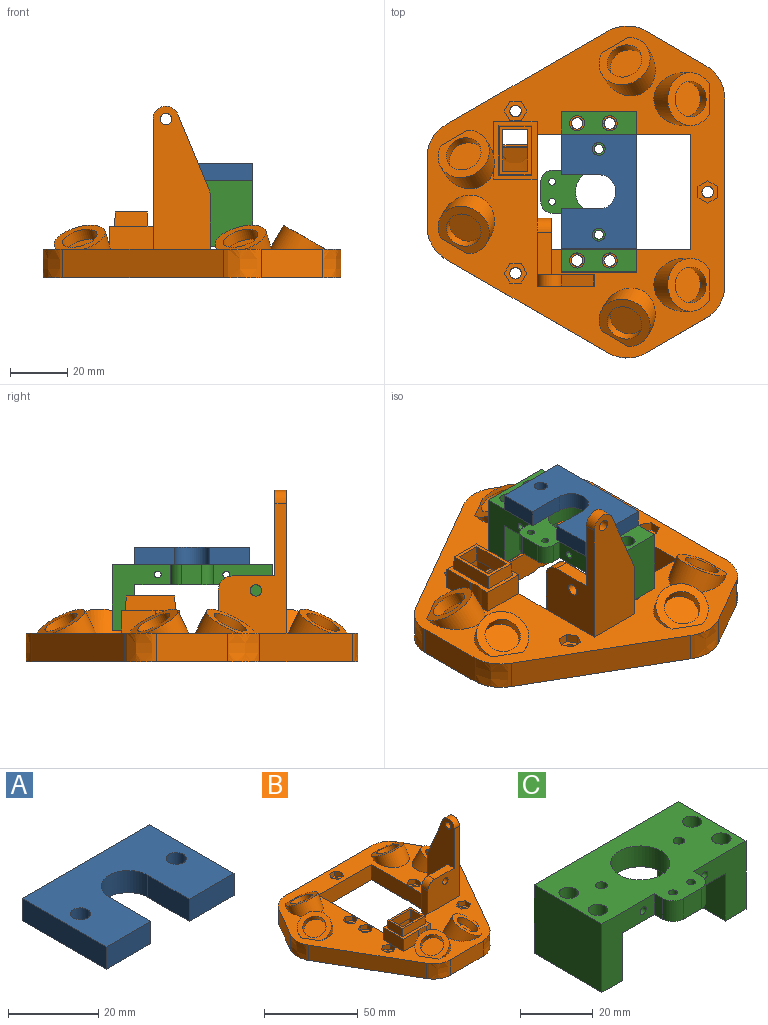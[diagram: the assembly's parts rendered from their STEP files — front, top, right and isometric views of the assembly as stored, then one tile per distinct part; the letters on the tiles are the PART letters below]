
ASSEMBLY  parts=3 mates=1
PART A: 12 faces, bbox 40x26.4x6 mm
  f0: plane 26.4x6mm, normal (1,0,0), area 158.4mm2, adj f1,f9,f10,f11
  f1: plane 40x6mm, normal (0,1,0), area 240mm2, adj f0,f2,f10,f11
  f2: plane 26.4x6mm, normal (-1,0,0), area 158.4mm2, adj f1,f3,f10,f11
  f3: plane 14x6mm, normal (0,-1,0), area 84mm2, adj f2,f4,f10,f11
  f4: plane 13.1x6mm, normal (1,0,0), area 78.6mm2, adj f3,f5,f10,f11
  f5: cylinder r=6mm len=12mm, axis (0,0,-1), area 113.1mm2, adj f4,f6,f10,f11
  f6: plane 13.1x6mm, normal (-1,0,0), area 78.6mm2, adj f5,f9,f10,f11
  f7: cylinder r=2.25mm len=6mm, axis (0,0,-1), area 84.8mm2, adj f10,f11
  f8: cylinder r=2.25mm len=6mm, axis (0,0,-1), area 84.8mm2, adj f10,f11
  f9: plane 14x6mm, normal (0,-1,0), area 84mm2, adj f0,f6,f10,f11
  f10: plane 40x26.4mm, normal (0,0,1), area 810.4mm2, adj f0,f1,f2,f3,f4,f5,f6,f7
  f11: plane 40x26.4mm, normal (0,0,-1), area 810.4mm2, adj f0,f1,f2,f3,f4,f5,f6,f7
PART B: 152 faces, bbox 116.3x104.3x60.1 mm
  f0: plane 116.2x104.17mm, normal (0,0,-1), area 6072.4mm2, adj f3,f4,f11,f12,f25,f26,f27,f28
  f1: plane 30x19.8mm, normal (0,1,0), area 394.4mm2, adj f2,f6,f11,f131,f133,f137,f139,f151
  f2: plane 25x5mm, normal (-1,0,0), area 100mm2, adj f1,f56,f130,f139,f151
  f3: plane 40.77x15.6mm, normal (0,-1,0), area 204.9mm2, adj f0,f68,f77,f146,f147,f148
  f4: plane 18.03x15.6mm, normal (0,1,0), area 165.4mm2, adj f0,f66,f74,f143,f144,f150
  f5: extruded ~5.77x0.35mm, area 1.4mm2, adj f74,f145
  f6: plane 116.2x104.17mm, normal (0,0,1), area 4334.7mm2, adj f1,f11,f12,f13,f14,f15,f16,f17
  f7: cylinder r=2mm len=4.4mm, axis (0,0,1), area 55.3mm2, adj f52,f101
  f8: cylinder r=2mm len=4.4mm, axis (0,0,1), area 55.3mm2, adj f51,f94
  f9: cylinder r=2mm len=4.4mm, axis (0,0,1), area 55.3mm2, adj f50,f122
  f10: cylinder r=2mm len=4.4mm, axis (0,0,1), area 55.3mm2, adj f49,f129
  f11: plane 48.72x10mm, normal (-1,0,0), area 484.5mm2, adj f0,f1,f6,f51,f52,f142
  f12: plane 53.72x10mm, normal (1,0,0), area 534.5mm2, adj f0,f6,f49,f50,f56,f142
  f13: cylinder r=9.25mm len=20.89mm, axis (-0.43,-0.25,0.87), area 260.4mm2, adj f6,f14
  f14: plane 17.91x16.67mm, normal (-0.43,-0.25,0.87), area 133.6mm2, adj f6,f13,f47
  f15: cylinder r=9.25mm len=19.41mm, axis (0,0.5,0.87), area 260.4mm2, adj f6,f16
  f16: plane 18.5x14.54mm, normal (0,0.5,0.87), area 133.6mm2, adj f6,f15,f45
  f17: cylinder r=9.25mm len=19.41mm, axis (0,0.5,0.87), area 260.4mm2, adj f6,f18
  f18: plane 18.5x14.54mm, normal (0,0.5,0.87), area 133.6mm2, adj f6,f17,f43
  f19: cylinder r=9.25mm len=20.89mm, axis (0.43,-0.25,0.87), area 260.4mm2, adj f6,f20
  f20: plane 17.91x16.67mm, normal (0.43,-0.25,0.87), area 133.6mm2, adj f6,f19,f41
  f21: cylinder r=9.25mm len=20.88mm, axis (-0.43,-0.25,0.87), area 260.4mm2, adj f6,f22,f54
  f22: plane 17.91x16.67mm, normal (-0.43,-0.25,0.87), area 133.6mm2, adj f6,f21,f39
  f23: cylinder r=9.25mm len=20.89mm, axis (0.43,-0.25,0.87), area 260.4mm2, adj f6,f24
  f24: plane 17.91x16.67mm, normal (0.43,-0.25,0.87), area 133.6mm2, adj f6,f23,f37
  f25: plane 56.29x32.5mm, normal (-0.87,-0.5,0), area 650mm2, adj f0,f6,f26,f36
  f26: extruded ~11.27x10mm, area 137.8mm2, adj f0,f6,f25,f27
  f27: plane 24.87x10mm, normal (0,-1,0), area 248.7mm2, adj f0,f6,f26,f28
  f28: extruded ~11.27x10mm, area 137.8mm2, adj f0,f6,f27,f29
  f29: plane 56.29x32.5mm, normal (0.87,-0.5,0), area 650mm2, adj f0,f6,f28,f30
  f30: extruded ~13.16x10mm, area 137.8mm2, adj f0,f6,f29,f31
  f31: plane 21.54x12.43mm, normal (0.87,0.5,0), area 248.7mm2, adj f0,f6,f30,f32
  f32: extruded ~11.53x10mm, area 137.8mm2, adj f0,f6,f31,f33
  f33: plane 65x10mm, normal (0,1,0), area 650mm2, adj f0,f6,f32,f34
  f34: extruded ~11.53x10mm, area 137.8mm2, adj f0,f6,f33,f35
  f35: plane 21.54x12.43mm, normal (-0.87,0.5,0), area 248.7mm2, adj f0,f6,f34,f36
  f36: extruded ~13.16x10mm, area 137.8mm2, adj f0,f6,f25,f35
  f37: cylinder r=6.25mm len=13.1mm, axis (0.43,-0.25,0.87), area 157.1mm2, adj f24,f38
  f38: plane 12.1x11.27mm, normal (0.43,-0.25,0.87), area 122.7mm2, adj f37
  f39: cylinder r=6.25mm len=13.1mm, axis (-0.43,-0.25,0.87), area 157.1mm2, adj f22,f40
  f40: plane 12.1x11.27mm, normal (-0.43,-0.25,0.87), area 122.7mm2, adj f39
  f41: cylinder r=6.25mm len=13.1mm, axis (0.43,-0.25,0.87), area 157.1mm2, adj f20,f42
  f42: plane 12.1x11.27mm, normal (0.43,-0.25,0.87), area 122.7mm2, adj f41
  f43: cylinder r=6.25mm len=12.83mm, axis (0,0.5,0.87), area 157.1mm2, adj f18,f44
  f44: plane 12.5x10.83mm, normal (0,0.5,0.87), area 122.7mm2, adj f43
  f45: cylinder r=6.25mm len=12.83mm, axis (0,0.5,0.87), area 157.1mm2, adj f16,f46
  f46: plane 12.5x10.83mm, normal (0,0.5,0.87), area 122.7mm2, adj f45
  f47: cylinder r=6.25mm len=13.1mm, axis (-0.43,-0.25,0.87), area 157.1mm2, adj f14,f48
  f48: plane 12.1x11.27mm, normal (-0.43,-0.25,0.87), area 122.7mm2, adj f47
  f49: cone r=2mm half-angle=45deg, axis (0,0,-1), area 70.2mm2, adj f0,f10,f12
  f50: cone r=2mm half-angle=45deg, axis (0,0,-1), area 70.2mm2, adj f0,f9,f12
  f51: cone r=2mm half-angle=45deg, axis (0,0,-1), area 70.2mm2, adj f0,f8,f11
  f52: cone r=2mm half-angle=45deg, axis (0,0,-1), area 70.2mm2, adj f0,f7,f11
  f53: plane 11.65x8mm, normal (0,-1,0), area 93.2mm2, adj f6,f54,f57,f59
  f54: extruded ~8x5.47mm, area 44.2mm2, adj f21,f53,f55,f59
  f55: plane 8x2.99mm, normal (0,-1,0), area 23.9mm2, adj f6,f54,f58,f59
  f56: plane 33.8x18mm, normal (0,1,0), area 452.9mm2, adj f0,f2,f6,f12,f57,f58,f59
  f57: plane 15.3x8mm, normal (-1,0,0), area 122.4mm2, adj f6,f53,f56,f59
  f58: plane 15.3x8mm, normal (1,0,0), area 122.4mm2, adj f6,f55,f56,f59
  f59: plane 20.11x15.3mm, normal (0,0,1), area 102.1mm2, adj f53,f54,f55,f56,f57,f58,f60,f61
  f60: plane 17.49x5mm, normal (0,-1,0.05), area 86.3mm2, adj f59,f61,f63,f64
  f61: plane 11.68x5mm, normal (1,0,0.05), area 57.2mm2, adj f59,f60,f62,f64
  f62: plane 17.49x5mm, normal (0,1,0.05), area 86.3mm2, adj f59,f61,f63,f64
  f63: plane 11.68x5mm, normal (-1,0,0.05), area 57.2mm2, adj f59,f60,f62,f64
  f64: plane 16.97x11.15mm, normal (0,0,1), area 61.8mm2, adj f60,f61,f62,f63,f70,f71,f72,f73
  f65: plane 18.03x15.6mm, normal (0,-1,0), area 165.4mm2, adj f0,f66,f77,f143,f144,f150
  f66: plane 12.9x5.6mm, normal (1,0,0), area 72.2mm2, adj f4,f65,f75,f144
  f67: plane 40.77x15.6mm, normal (0,1,0), area 204.9mm2, adj f0,f68,f74,f145,f146,f147,f148
  f68: plane 12.9x5.6mm, normal (-1,0,0), area 72.2mm2, adj f3,f67,f76,f146
  f69: plane 15.31x10.5mm, normal (0,0,-1), area 17.7mm2, adj f70,f71,f72,f73,f74,f75,f76,f77
  f70: plane 15.22x6.2mm, normal (0,1,-0.05), area 92.5mm2, adj f64,f69,f71,f73
  f71: plane 9.4x6.2mm, normal (-1,0,-0.05), area 56.4mm2, adj f64,f69,f70,f72
  f72: plane 15.22x6.2mm, normal (0,-1,-0.05), area 92.5mm2, adj f64,f69,f71,f73
  f73: plane 9.4x6.2mm, normal (1,0,-0.05), area 56.4mm2, adj f64,f69,f70,f72
  f74: plane 17.71x1.2mm, normal (0,0.71,-0.71), area 26.1mm2, adj f4,f5,f67,f69,f75,f76,f149
  f75: plane 12.9x1.2mm, normal (0.71,0,-0.71), area 19.9mm2, adj f66,f69,f74,f77
  f76: plane 12.9x1.2mm, normal (-0.71,0,-0.71), area 19.9mm2, adj f68,f69,f74,f77
  f77: plane 17.71x1.2mm, normal (0,-0.71,-0.71), area 28mm2, adj f3,f65,f69,f75,f76,f149
  f78: cylinder r=2mm len=6.9mm, axis (0,0,1), area 86.7mm2, adj f0,f108
  f79: cylinder r=2mm len=6.9mm, axis (0,0,1), area 86.7mm2, adj f0,f87
  f80: cylinder r=2mm len=6.9mm, axis (0,0,1), area 86.7mm2, adj f0,f115
  f81: plane 3.4x3.1mm, normal (-0.5,-0.87,0), area 12.2mm2, adj f6,f82,f86,f87
  f82: plane 3.4x3.1mm, normal (0.5,-0.87,0), area 12.2mm2, adj f6,f81,f83,f87
  f83: plane 3.93x3.1mm, normal (1,0,0), area 12.2mm2, adj f6,f82,f84,f87
  f84: plane 3.4x3.1mm, normal (0.5,0.87,0), area 12.2mm2, adj f6,f83,f85,f87
  f85: plane 3.4x3.1mm, normal (-0.5,0.87,0), area 12.2mm2, adj f6,f84,f86,f87
  f86: plane 3.93x3.1mm, normal (-1,0,0), area 12.2mm2, adj f6,f81,f85,f87
  f87: plane 7.85x6.8mm, normal (0,0,1), area 27.5mm2, adj f79,f81,f82,f83,f84,f85,f86
  f88: plane 3.93x3.1mm, normal (-1,0,0), area 12.2mm2, adj f6,f89,f93,f94
  f89: plane 3.4x3.1mm, normal (-0.5,-0.87,0), area 12.2mm2, adj f6,f88,f90,f94
  f90: plane 3.4x3.1mm, normal (0.5,-0.87,0), area 12.2mm2, adj f6,f89,f91,f94
  f91: plane 3.93x3.1mm, normal (1,0,0), area 12.2mm2, adj f6,f90,f92,f94
  f92: plane 3.4x3.1mm, normal (0.5,0.87,0), area 12.2mm2, adj f6,f91,f93,f94
  f93: plane 3.4x3.1mm, normal (-0.5,0.87,0), area 12.2mm2, adj f6,f88,f92,f94
  f94: plane 7.85x6.8mm, normal (0,0,1), area 27.5mm2, adj f8,f88,f89,f90,f91,f92,f93
  f95: plane 3.93x3.1mm, normal (-1,0,0), area 12.2mm2, adj f6,f96,f100,f101
  f96: plane 3.4x3.1mm, normal (-0.5,-0.87,0), area 12.2mm2, adj f6,f95,f97,f101
  f97: plane 3.4x3.1mm, normal (0.5,-0.87,0), area 12.2mm2, adj f6,f96,f98,f101
  f98: plane 3.93x3.1mm, normal (1,0,0), area 12.2mm2, adj f6,f97,f99,f101
  f99: plane 3.4x3.1mm, normal (0.5,0.87,0), area 12.2mm2, adj f6,f98,f100,f101
  f100: plane 3.4x3.1mm, normal (-0.5,0.87,0), area 12.2mm2, adj f6,f95,f99,f101
  f101: plane 7.85x6.8mm, normal (0,0,1), area 27.5mm2, adj f7,f95,f96,f97,f98,f99,f100
  f102: plane 3.4x3.1mm, normal (-0.87,0.5,0), area 12.2mm2, adj f6,f103,f107,f108
  f103: plane 3.4x3.1mm, normal (-0.87,-0.5,0), area 12.2mm2, adj f6,f102,f104,f108
  f104: plane 3.93x3.1mm, normal (0,-1,0), area 12.2mm2, adj f6,f103,f105,f108
  f105: plane 3.4x3.1mm, normal (0.87,-0.5,0), area 12.2mm2, adj f6,f104,f106,f108
  f106: plane 3.4x3.1mm, normal (0.87,0.5,0), area 12.2mm2, adj f6,f105,f107,f108
  f107: plane 3.93x3.1mm, normal (0,1,0), area 12.2mm2, adj f6,f102,f106,f108
  f108: plane 7.85x6.8mm, normal (0,0,1), area 27.5mm2, adj f78,f102,f103,f104,f105,f106,f107
  f109: plane 3.4x3.1mm, normal (0.5,0.87,0), area 12.2mm2, adj f6,f110,f114,f115
  f110: plane 3.4x3.1mm, normal (-0.5,0.87,0), area 12.2mm2, adj f6,f109,f111,f115
  f111: plane 3.93x3.1mm, normal (-1,0,0), area 12.2mm2, adj f6,f110,f112,f115
  f112: plane 3.4x3.1mm, normal (-0.5,-0.87,0), area 12.2mm2, adj f6,f111,f113,f115
  f113: plane 3.4x3.1mm, normal (0.5,-0.87,0), area 12.2mm2, adj f6,f112,f114,f115
  f114: plane 3.93x3.1mm, normal (1,0,0), area 12.2mm2, adj f6,f109,f113,f115
  f115: plane 7.85x6.8mm, normal (0,0,1), area 27.5mm2, adj f80,f109,f110,f111,f112,f113,f114
  f116: plane 3.93x3.1mm, normal (1,0,0), area 12.2mm2, adj f6,f117,f121,f122
  f117: plane 3.4x3.1mm, normal (0.5,0.87,0), area 12.2mm2, adj f6,f116,f118,f122
  f118: plane 3.4x3.1mm, normal (-0.5,0.87,0), area 12.2mm2, adj f6,f117,f119,f122
  f119: plane 3.93x3.1mm, normal (-1,0,0), area 12.2mm2, adj f6,f118,f120,f122
  f120: plane 3.4x3.1mm, normal (-0.5,-0.87,0), area 12.2mm2, adj f6,f119,f121,f122
  f121: plane 3.4x3.1mm, normal (0.5,-0.87,0), area 12.2mm2, adj f6,f116,f120,f122
  f122: plane 7.85x6.8mm, normal (0,0,1), area 27.5mm2, adj f9,f116,f117,f118,f119,f120,f121
  f123: plane 3.93x3.1mm, normal (1,0,0), area 12.2mm2, adj f6,f124,f128,f129
  f124: plane 3.4x3.1mm, normal (0.5,0.87,0), area 12.2mm2, adj f6,f123,f125,f129
  f125: plane 3.4x3.1mm, normal (-0.5,0.87,0), area 12.2mm2, adj f6,f124,f126,f129
  f126: plane 3.93x3.1mm, normal (-1,0,0), area 12.2mm2, adj f6,f125,f127,f129
  f127: plane 3.4x3.1mm, normal (-0.5,-0.87,0), area 12.2mm2, adj f6,f126,f128,f129
  f128: plane 3.4x3.1mm, normal (0.5,-0.87,0), area 12.2mm2, adj f6,f123,f127,f129
  f129: plane 7.85x6.8mm, normal (0,0,1), area 27.5mm2, adj f10,f123,f124,f125,f126,f127,f128
  f130: plane 45.5x23.8mm, normal (0,-1,0), area 560.1mm2, adj f2,f6,f131,f133,f134,f136,f139,f140
  f131: plane 14.8x5mm, normal (0,0,1), area 74mm2, adj f1,f130,f133,f139
  f132: plane 19x4mm, normal (0,1,0), area 76mm2, adj f6,f133,f134,f138
  f133: plane 50x20mm, normal (-1,0,0), area 693.9mm2, adj f1,f6,f130,f131,f132,f135,f138,f140
  f134: plane 50x20mm, normal (1,0,0), area 793.9mm2, adj f6,f130,f132,f135,f138,f140,f141
  f135: plane 26.31x10.96mm, normal (0,0.92,0.38), area 114mm2, adj f133,f134,f138,f140
  f136: cylinder r=2mm len=4mm, axis (0,1,0), area 37.7mm2, adj f130,f137
  f137: cone r=2mm half-angle=45deg, axis (0,1,0), area 53.3mm2, adj f1,f136
  f138: cylinder r=5mm len=4mm, axis (-1,0,0), area 7.9mm2, adj f132,f133,f134,f135
  f139: cylinder r=5mm len=5mm, axis (0,1,0), area 39.3mm2, adj f1,f2,f130,f131
  f140: cylinder r=4.5mm len=8.65mm, axis (1,0,0), area 49.4mm2, adj f130,f133,f134,f135
  f141: cylinder r=2mm len=4mm, axis (1,0,0), area 50.3mm2, adj f133,f134
  f142: plane 40x10mm, normal (0,-1,0), area 400mm2, adj f0,f6,f11,f12
  f143: extruded ~12.9x10mm, area 186.2mm2, adj f0,f4,f65,f150
  f144: extruded ~12.9x10mm, area 131.2mm2, adj f0,f4,f65,f66
  f145: plane 5.86x0.44mm, normal (0,0,-1), area 1.3mm2, adj f5,f67
  f146: extruded ~30.69x12.9mm, area 427.7mm2, adj f0,f3,f67,f68
  f147: extruded ~20.74x12.9mm, area 307.3mm2, adj f0,f3,f67,f148
  f148: plane 12.9x5.6mm, normal (1,0,0), area 72.2mm2, adj f3,f67,f147,f149
  f149: plane 12.9x0.8mm, normal (0,0,1), area 10.3mm2, adj f74,f77,f148,f150
  f150: plane 12.9x5.6mm, normal (-1,0,0), area 72.2mm2, adj f4,f65,f143,f149
  f151: plane 10.8x10mm, normal (-0.38,0.83,-0.41), area 65.3mm2, adj f0,f1,f2
PART C: 41 faces, bbox 56x33.6x23 mm
  f0: plane 40x33.6mm, normal (0,0,-1), area 857.1mm2, adj f1,f3,f5,f6,f7,f8,f9,f13
  f1: plane 23x20.54mm, normal (0,-1,0), area 267.3mm2, adj f0,f2,f13,f18,f21,f22,f23
  f2: plane 26.4x23mm, normal (1,0,0), area 607.2mm2, adj f1,f3,f18,f22
  f3: plane 56x23mm, normal (0,1,0), area 639mm2, adj f0,f2,f4,f18,f19,f20,f21,f22
  f4: plane 26.4x23mm, normal (-1,0,0), area 607.2mm2, adj f3,f5,f18,f20
  f5: plane 23x20.46mm, normal (0,-1,0), area 266.7mm2, adj f0,f4,f6,f18,f19,f20,f24
  f6: plane 7x3.2mm, normal (-1,0,0), area 22.4mm2, adj f0,f5,f7,f18
  f7: cylinder r=4mm len=7mm, axis (0,0,-1), area 44mm2, adj f0,f6,f8,f18
  f8: plane 7x7mm, normal (0,-1,0), area 49mm2, adj f0,f7,f9,f18
  f9: cylinder r=4mm len=7mm, axis (0,0,-1), area 44mm2, adj f0,f8,f13,f18
  f10: cylinder r=2.65mm len=23mm, axis (0,0,-1), area 383mm2, adj f18,f22
  f11: cylinder r=2.65mm len=23mm, axis (0,0,-1), area 383mm2, adj f18,f20
  f12: cylinder r=2.65mm len=23mm, axis (0,0,-1), area 383mm2, adj f18,f20
  f13: plane 7x3.2mm, normal (1,0,0), area 22.4mm2, adj f0,f1,f9,f18
  f14: cylinder r=1.2mm len=7mm, axis (0,0,-1), area 52.8mm2, adj f0,f18
  f15: cylinder r=1.2mm len=7mm, axis (0,0,-1), area 52.8mm2, adj f0,f18
  f16: cylinder r=8.1mm len=16.2mm, axis (0,0,-1), area 356.3mm2, adj f0,f18
  f17: cylinder r=2.65mm len=23mm, axis (0,0,-1), area 383mm2, adj f18,f22
  f18: plane 56x33.6mm, normal (0,0,1), area 1260mm2, adj f1,f2,f3,f4,f5,f6,f7,f8
  f19: plane 26.4x16mm, normal (1,0,0), area 422.4mm2, adj f0,f3,f5,f20
  f20: plane 26.4x8mm, normal (0,0,-1), area 167.1mm2, adj f3,f4,f5,f11,f12,f19
  f21: plane 26.4x16mm, normal (-1,0,0), area 422.4mm2, adj f0,f1,f3,f22
  f22: plane 26.4x8mm, normal (0,0,-1), area 167.1mm2, adj f1,f2,f3,f10,f17,f21
  f23: cylinder r=1.2mm len=26.4mm, axis (0,1,0), area 199.1mm2, adj f1,f3
  f24: cylinder r=1.2mm len=26.4mm, axis (0,1,0), area 199.1mm2, adj f3,f5
  f25: cylinder r=1.6mm len=5mm, axis (0,0,1), area 50.3mm2, adj f18,f34
  f26: cylinder r=1.6mm len=5mm, axis (0,0,1), area 50.3mm2, adj f18,f27
  f27: plane 8.08x7mm, normal (0,0,-1), area 34.4mm2, adj f26,f28,f29,f30,f31,f32,f33
  f28: plane 3.5x2.02mm, normal (0.5,0.87,0), area 8.1mm2, adj f0,f27,f29,f33
  f29: plane 3.5x2.02mm, normal (-0.5,0.87,0), area 8.1mm2, adj f0,f27,f28,f30
  f30: plane 4.04x2mm, normal (-1,0,0), area 8.1mm2, adj f0,f27,f29,f31
  f31: plane 3.5x2.02mm, normal (-0.5,-0.87,0), area 8.1mm2, adj f0,f27,f30,f32
  f32: plane 3.5x2.02mm, normal (0.5,-0.87,0), area 8.1mm2, adj f0,f27,f31,f33
  f33: plane 4.04x2mm, normal (1,0,0), area 8.1mm2, adj f0,f27,f28,f32
  f34: plane 8.08x7mm, normal (0,0,-1), area 34.4mm2, adj f25,f35,f36,f37,f38,f39,f40
  f35: plane 3.5x2.02mm, normal (-0.5,-0.87,0), area 8.1mm2, adj f0,f34,f36,f40
  f36: plane 3.5x2.02mm, normal (0.5,-0.87,0), area 8.1mm2, adj f0,f34,f35,f37
  f37: plane 4.04x2mm, normal (1,0,0), area 8.1mm2, adj f0,f34,f36,f38
  f38: plane 3.5x2.02mm, normal (0.5,0.87,0), area 8.1mm2, adj f0,f34,f37,f39
  f39: plane 3.5x2.02mm, normal (-0.5,0.87,0), area 8.1mm2, adj f0,f34,f38,f40
  f40: plane 4.04x2mm, normal (-1,0,0), area 8.1mm2, adj f0,f34,f35,f39
PLACE A rot(axis=(0,0,-1),90deg) t=(-5.31,2.57,63.43)mm
PLACE B rot(axis=(0,0,-1),90deg) t=(-5.31,2.57,36.43)mm
PLACE C rot(axis=(0,0,-1),90deg) t=(-5.31,2.57,63.43)mm
MATE fastened A.f7 <-> C.f25  axis (0,0,-1) through (-3.31,17.57,70.43)mm
